# Revit family: DP
name_source: partatom
category: Lighting Fixtures
revit_build: Autodesk Revit 2014 (Build: 20130308_1515(x64)
units: mm (PartAtom-declared; Revit-internal decimal feet)

## types (3) — shared parameters
Apparent Load = 8 VA
Assembly Code = D5020200
Color Filter = 16777215
Connector Description = Lighting Connector
Default Elevation = 48"
Description = Security Lighting's Drum Pendant Series offers a classic pendant shape in multiple sizes and colors to provide maximum design flexibility for all of today's contemporary decors.
Dimming Lamp Color Temperature Shift = <None>
Emit Shape Visible in Rendering = No
Fixture distribution = Direct
Housing Material = Paint - Hubbell - Matte White
Lamp = LED
Load Classification = Lighting
Manufacturer = Security Lighting
Photometric Web File = generic
Power Factor = 1
Product Documentation Link = https://hubbellcdn.com
Product Link = https://www.hubbell.com
Reflector Finish = Hubbell - White Glass
Tilt Angle = 60.00°
URL = https://www.hubbell.com
Voltage = 120 V
Warranty = 5 years Warranty
Wattage Comments = 8W
Watts = 8 W

## per-type parameters (varying)
| type | Drum-Height | Emit from Circle Diameter | LF |
| S-D-P | 8 1/2" | 13 3/4" | DP : S |
| M-D-P | 14" | 21 3/4" | DP : M |
| L-D-P | 14" | 29 3/4" | DP : L |

note: column(s) folded — value = type name in every type: Model

## geometry (parser evidence)
native form markers: Blend x15, Sweep x4
no freeform markers — native parametric forms only
